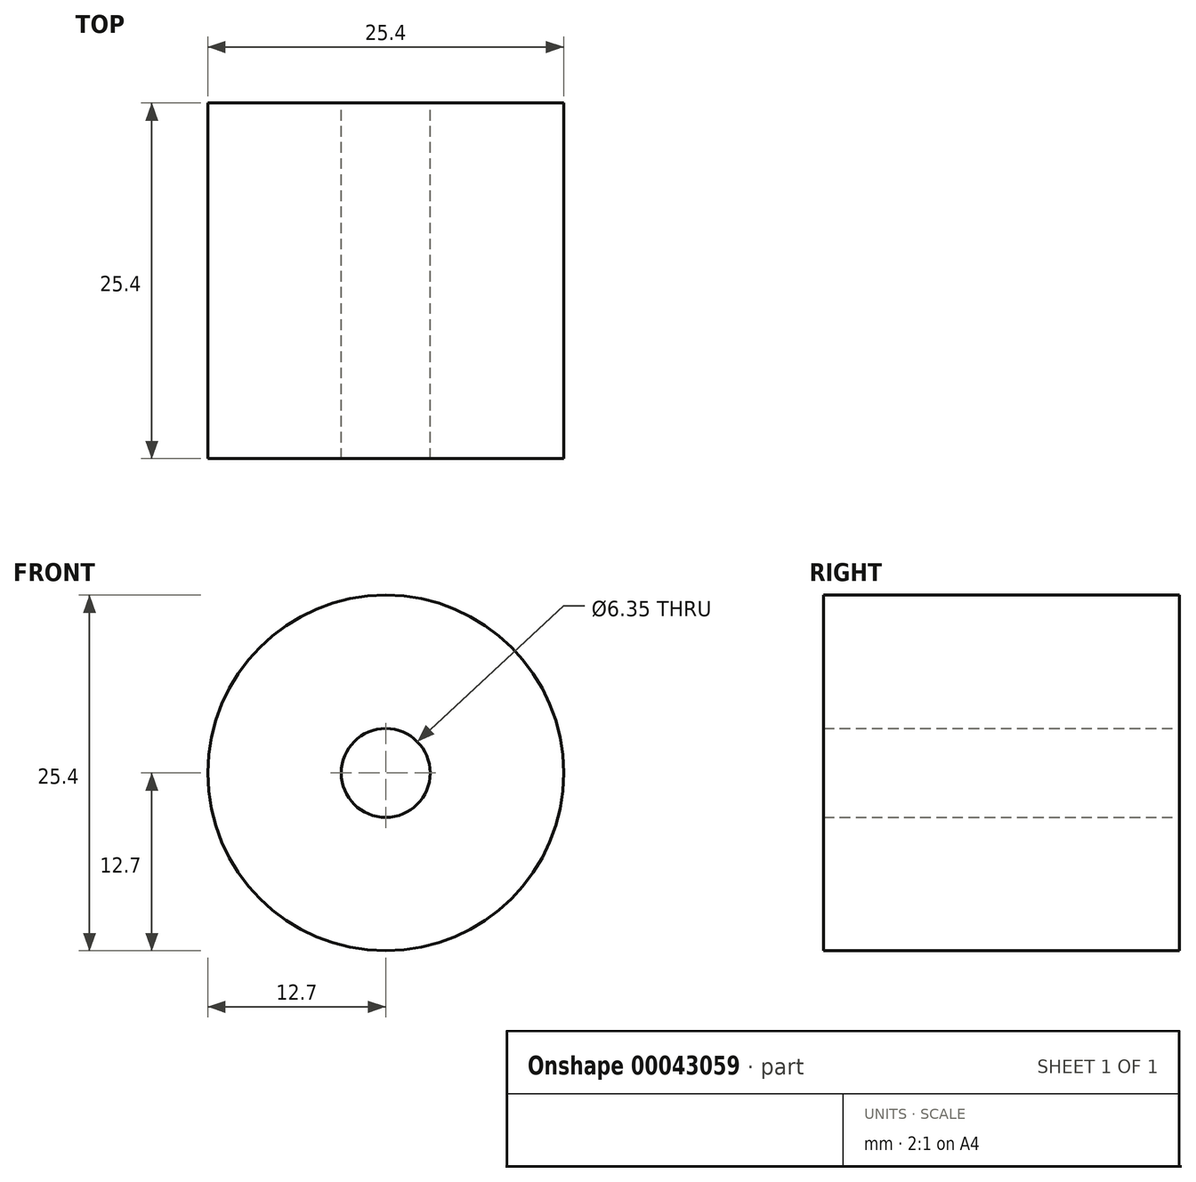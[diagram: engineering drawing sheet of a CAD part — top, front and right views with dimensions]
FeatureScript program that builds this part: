
annotation { "Feature Type Name" : "Feature", "Feature Type Description" : "" }
export const myFeature = defineFeature(function(context is Context, id is Id, definition is map)
    precondition{}
    {
        {
            var Q0;
            Q0=qCreatedBy(makeId("Front.planeOp"),FACE);
            var sketch = newSketch(context, id + "F0", { "sketchPlane" : qUnion([Q0])});
            skCircle(sketch, "E0", {"center": v(0, 0) * mm, "radius": 12.7 * mm});
            skCircle(sketch, "E1", {"center": v(0, 0) * mm, "radius": 3.18 * mm});
            skSolve(sketch);
        }
        {
            var Q0;
            Q0 = qSketchRegion(id + "F0", true);
            extrude(context, id + "F1", {"entities" : qUnion([Q0]), "depth" : 25.4 * mm});
        }
    });
